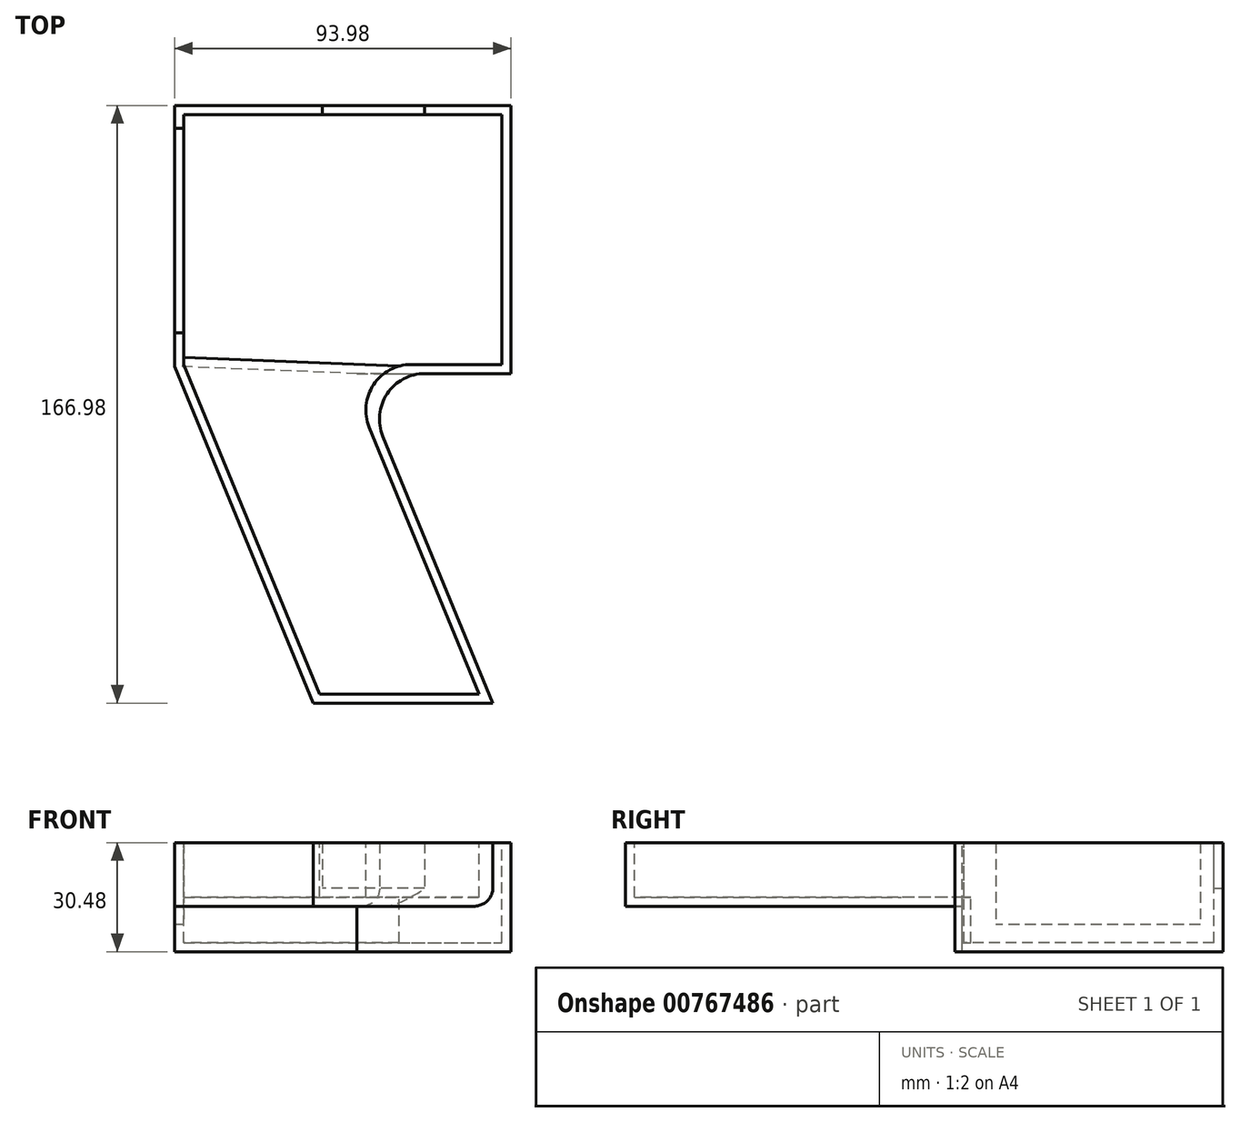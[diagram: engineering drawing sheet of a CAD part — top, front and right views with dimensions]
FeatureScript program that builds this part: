
annotation { "Feature Type Name" : "Feature", "Feature Type Description" : "" }
export const myFeature = defineFeature(function(context is Context, id is Id, definition is map)
    precondition{}
    {
        {
            var Q0;
            Q0=qCreatedBy(makeId("Top.planeOp"),FACE);
            var sketch = newSketch(context, id + "F0", { "sketchPlane" : qUnion([Q0])});
            skLineSegment(sketch, "E0.bottom", {"start": v(-51.18, 81.23) * mm, "end": v(37.72, 81.23) * mm});
            skLineSegment(sketch, "E0.top", {"start": v(-6.55, 11.38) * mm, "end": v(37.72, 11.38) * mm});
            skLineSegment(sketch, "E0.left", {"start": v(-51.18, 81.23) * mm, "end": v(-51.18, 11.38) * mm});
            skLineSegment(sketch, "E0.right", {"start": v(37.72, 81.23) * mm, "end": v(37.72, 11.38) * mm});
            skLineSegment(sketch, "E1", {"start": v(-51.18, 11.38) * mm, "end": v(-13.27, -80.67) * mm});
            skLineSegment(sketch, "E2", {"start": v(-13.27, -80.67) * mm, "end": v(31.37, -80.67) * mm});
            skLineSegment(sketch, "E3", {"start": v(31.37, -80.67) * mm, "end": v(-6.55, 11.38) * mm});
            skPoint(sketch, "E4.end.orphan", {"position": v(24.9, -64.95) * mm});
            skLineSegment(sketch, "E5.0", {"start": v(-53.72, 83.77) * mm, "end": v(-53.72, 10.88) * mm});
            skLineSegment(sketch, "E5.1", {"start": v(-53.72, 10.88) * mm, "end": v(-14.97, -83.2) * mm});
            skLineSegment(sketch, "E5.2", {"start": v(40.26, 83.77) * mm, "end": v(40.26, 8.84) * mm});
            skLineSegment(sketch, "E5.3", {"start": v(-2.75, 8.84) * mm, "end": v(40.26, 8.84) * mm});
            skLineSegment(sketch, "E5.4", {"start": v(35.16, -83.2) * mm, "end": v(-2.75, 8.84) * mm});
            skLineSegment(sketch, "E5.5", {"start": v(-53.72, 83.77) * mm, "end": v(40.26, 83.77) * mm});
            skLineSegment(sketch, "E5.6", {"start": v(-14.97, -83.2) * mm, "end": v(35.16, -83.2) * mm});
            skSolve(sketch);
        }
        {
            var Q0;
            Q0=makeQuery(id+"F0.imprint","IMPRINT",FACE,{"disambiguationData":[TD([[makeQuery(id+"F0.imprint","IMPRINT",EDGE,{"derivedFrom":sQuery(id+"F0.wireOp",EDGE,"E0.bottom")}),1.0]])]});
            var Q1;
            Q1=makeQuery(id+"F0.imprint","IMPRINT",FACE,{"disambiguationData":[TD([[makeQuery(id+"F0.imprint","IMPRINT",EDGE,{"derivedFrom":sQuery(id+"F0.wireOp",EDGE,"E0.bottom")}),-1.0]])]});
            extrude(context, id + "F1", {"entities" : qUnion([Q0, Q1]), "oppositeDirection" : true, "depth" : 17.78 * mm, "offsetDistance" : 25.4 * mm});
        }
        {
            var Q0;
            Q0=makeQuery(id+"F1.opExtrude","CAP_FACE",FACE,{"disambiguationData":[OSD([sQuery(id+"F0.wireOp",EDGE,"E5.0"),sQuery(id+"F0.wireOp",EDGE,"E5.1"),sQuery(id+"F0.wireOp",EDGE,"E5.2"),sQuery(id+"F0.wireOp",EDGE,"E5.3"),sQuery(id+"F0.wireOp",EDGE,"E5.4"),sQuery(id+"F0.wireOp",EDGE,"E5.5"),sQuery(id+"F0.wireOp",EDGE,"E5.6")])],"isStart":false});
            var sketch = newSketch(context, id + "F2", { "sketchPlane" : qUnion([Q0])});
            skLineSegment(sketch, "E6", {"start": v(-2.75, -8.84) * mm, "end": v(-53.72, -10.88) * mm});
            skSolve(sketch);
        }
        {
            var Q0;
            Q0=makeQuery(id+"F2.imprint","IMPRINT",FACE,{"disambiguationData":[TD([[makeQuery(id+"F2.imprint","IMPRINT",EDGE,{"derivedFrom":sQuery(id+"F2.wireOp",EDGE,"E6")}),1.0]])]});
            extrude(context, id + "F3", {"entities" : qUnion([Q0]), "operationType" : NewBodyOperationType.ADD, "depth" : 12.7 * mm, "offsetDistance" : 25.4 * mm});
        }
        {
            var Q0;
            Q0=makeQuery(id+"F1.opExtrude","CAP_FACE",FACE,{"disambiguationData":[OSD([sQuery(id+"F0.wireOp",EDGE,"E5.0"),sQuery(id+"F0.wireOp",EDGE,"E5.1"),sQuery(id+"F0.wireOp",EDGE,"E5.2"),sQuery(id+"F0.wireOp",EDGE,"E5.3"),sQuery(id+"F0.wireOp",EDGE,"E5.4"),sQuery(id+"F0.wireOp",EDGE,"E5.5"),sQuery(id+"F0.wireOp",EDGE,"E5.6")])],"isStart":true});
            shell(context, id + "F4", {"entities" : qUnion([Q0]), "thickness" : 2.54 * mm});
        }
        {
            var Q0;
            Q0=makeQuery(id+"F3.opExtrude","CAP_EDGE",EDGE,{"disambiguationData":[OSD([sQuery(id+"F2.wireOp",EDGE,"E6")])],"isStart":true});
            var Q1;
            Q1=makeQuery(id+"F1.opExtrude","SWEPT_EDGE",EDGE,{"disambiguationData":[OSD([sQuery(id+"F0.wireOp",EDGE,"E5.3"),sQuery(id+"F0.wireOp",EDGE,"E5.4")])]});
            var Q2;
            Q2=makeQuery(id+"F4.opShell","OFFSET_EDGE",EDGE,{"disambiguationData":[OSD([sQuery(id+"F0.wireOp",EDGE,"E5.3"),sQuery(id+"F0.wireOp",EDGE,"E5.4")])]});
            fillet(context, id + "F5", {"entities" : qUnion([Q0, Q1, Q2]), "radius" : 12.7 * mm, "tangentPropagation" : true, "allowEdgeOverflow" : false});
        }
        {
            var Q0;
            {var subQ0=sQuery(id+"F0.wireOp",EDGE,"E5.0");Q0=makeQuery(id+"F3.boolean.opBoolean","MERGE",FACE,{"derivedFrom":[makeQuery(id+"F1.opExtrude","SWEPT_FACE",FACE,{"disambiguationData":[OSD([subQ0])]}),makeQuery(id+"F3.opExtrude","SWEPT_FACE",FACE,{"disambiguationData":[OSD([subQ0])]})]});}
            var sketch = newSketch(context, id + "F6", { "sketchPlane" : qUnion([Q0])});
            skLineSegment(sketch, "E7.bottom", {"start": v(-77.44, 0) * mm, "end": v(-20.3, 0) * mm});
            skLineSegment(sketch, "E7.top", {"start": v(-77.44, -22.86) * mm, "end": v(-20.3, -22.86) * mm});
            skLineSegment(sketch, "E7.left", {"start": v(-77.44, 0) * mm, "end": v(-77.44, -22.86) * mm});
            skLineSegment(sketch, "E7.right", {"start": v(-20.3, 0) * mm, "end": v(-20.3, -22.86) * mm});
            skSolve(sketch);
        }
        {
            var Q0;
            Q0=makeQuery(id+"F6.imprint","IMPRINT",FACE,{"disambiguationData":[TD([[makeQuery(id+"F6.imprint","IMPRINT",EDGE,{"derivedFrom":sQuery(id+"F6.wireOp",EDGE,"E7.bottom")}),-1.0]])]});
            extrude(context, id + "F7", {"entities" : qUnion([Q0]), "operationType" : NewBodyOperationType.REMOVE, "oppositeDirection" : true, "depth" : 25.4 * mm, "offsetDistance" : 25.4 * mm});
        }
        {
            var Q0;
            {var subQ0=sQuery(id+"F0.wireOp",EDGE,"E5.5");Q0=makeQuery(id+"F3.boolean.opBoolean","MERGE",FACE,{"derivedFrom":[makeQuery(id+"F1.opExtrude","SWEPT_FACE",FACE,{"disambiguationData":[OSD([subQ0])]}),makeQuery(id+"F3.opExtrude","SWEPT_FACE",FACE,{"disambiguationData":[OSD([subQ0])]})]});}
            var sketch = newSketch(context, id + "F8", { "sketchPlane" : qUnion([Q0])});
            skLineSegment(sketch, "E8.bottom", {"start": v(-16.13, 0) * mm, "end": v(12.45, 0) * mm});
            skLineSegment(sketch, "E8.top", {"start": v(-16.13, -12.7) * mm, "end": v(12.45, -12.7) * mm});
            skLineSegment(sketch, "E8.left", {"start": v(-16.13, 0) * mm, "end": v(-16.13, -12.7) * mm});
            skLineSegment(sketch, "E8.right", {"start": v(12.45, 0) * mm, "end": v(12.45, -12.7) * mm});
            skSolve(sketch);
        }
        {
            var Q0;
            Q0=makeQuery(id+"F8.imprint","IMPRINT",FACE,{"disambiguationData":[TD([[makeQuery(id+"F8.imprint","IMPRINT",EDGE,{"derivedFrom":sQuery(id+"F8.wireOp",EDGE,"E8.bottom")}),1.0]])]});
            extrude(context, id + "F9", {"entities" : qUnion([Q0]), "operationType" : NewBodyOperationType.REMOVE, "oppositeDirection" : true, "depth" : 25.4 * mm, "offsetDistance" : 25.4 * mm});
        }
        {
            var Q0;
            Q0=makeQuery(id+"F1.opExtrude","CAP_EDGE",EDGE,{"disambiguationData":[OSD([sQuery(id+"F0.wireOp",EDGE,"E5.4")])],"isStart":false});
            fillet(context, id + "F10", {"entities" : qUnion([Q0]), "radius" : 4.9 * mm, "tangentPropagation" : true, "allowEdgeOverflow" : false});
        }
    });
